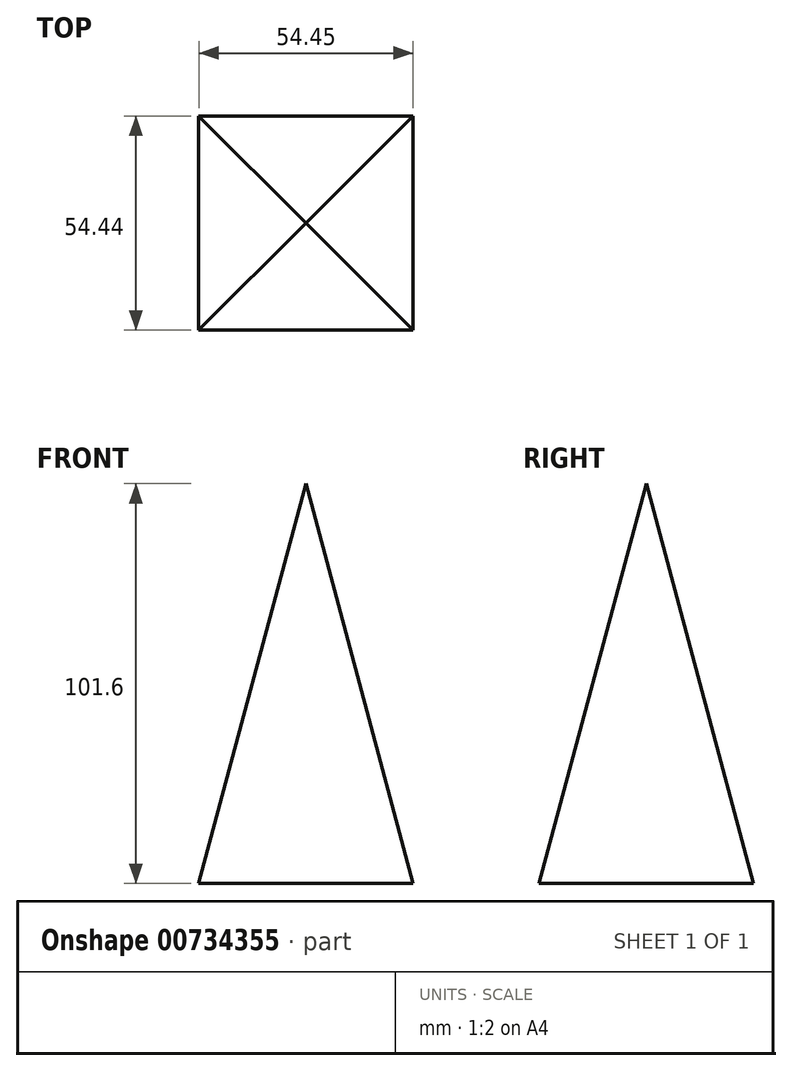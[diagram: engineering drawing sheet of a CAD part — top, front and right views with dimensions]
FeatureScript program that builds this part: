
annotation { "Feature Type Name" : "Feature", "Feature Type Description" : "" }
export const myFeature = defineFeature(function(context is Context, id is Id, definition is map)
    precondition{}
    {
        {
            var Q0;
            Q0=qCreatedBy(makeId("Top.planeOp"),FACE);
            var sketch = newSketch(context, id + "F0", { "sketchPlane" : qUnion([Q0])});
            skLineSegment(sketch, "E0.bottom", {"start": v(-45.07, 43.32) * mm, "end": v(43.83, 43.32) * mm});
            skLineSegment(sketch, "E0.top", {"start": v(-45.07, -45.58) * mm, "end": v(43.83, -45.58) * mm});
            skLineSegment(sketch, "E0.left", {"start": v(-45.07, 43.32) * mm, "end": v(-45.07, -45.58) * mm});
            skLineSegment(sketch, "E0.right", {"start": v(43.83, 43.32) * mm, "end": v(43.83, -45.58) * mm});
            skSolve(sketch);
        }
        {
            var Q0;
            Q0=qSketchRegion(id+"F0",true);
            extrude(context, id + "F1", {"entities" : qUnion([Q0]), "depth" : 101.6 * mm});
        }
        {
            var Q0;
            Q0=makeQuery(id+"F1.opExtrude","CAP_EDGE",EDGE,{"disambiguationData":[OSD([sQuery(id+"F0.wireOp",EDGE,"E0.top")])],"isStart":false});
            var Q1;
            Q1=makeQuery(id+"F1.opExtrude","CAP_EDGE",EDGE,{"disambiguationData":[OSD([sQuery(id+"F0.wireOp",EDGE,"E0.bottom")])],"isStart":false});
            var Q2;
            Q2=makeQuery(id+"F1.opExtrude","CAP_EDGE",EDGE,{"disambiguationData":[OSD([sQuery(id+"F0.wireOp",EDGE,"E0.left")])],"isStart":false});
            var Q3;
            Q3=makeQuery(id+"F1.opExtrude","CAP_EDGE",EDGE,{"disambiguationData":[OSD([sQuery(id+"F0.wireOp",EDGE,"E0.right")])],"isStart":false});
            chamfer(context, id + "F2", {"entities" : qUnion([Q0, Q1, Q2, Q3]), "chamferType" : ChamferType.OFFSET_ANGLE, "width" : 44.45 * mm, "oppositeDirection" : false, "angle" : 75 * degree, "tangentPropagation" : true});
        }
    });
